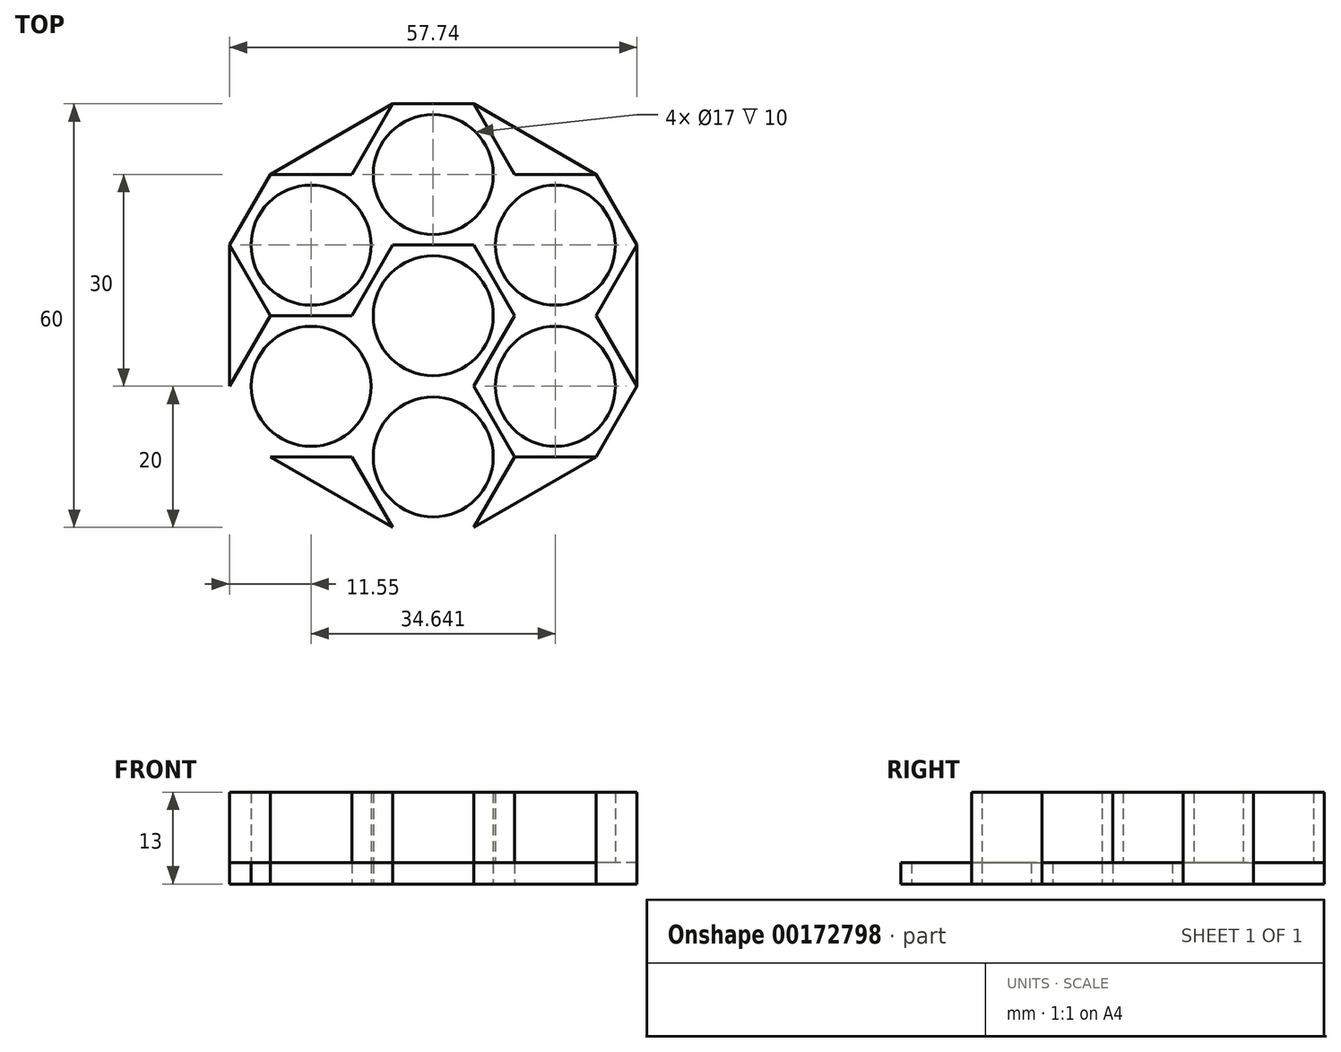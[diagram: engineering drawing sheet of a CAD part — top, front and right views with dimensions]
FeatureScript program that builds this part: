
annotation { "Feature Type Name" : "Feature", "Feature Type Description" : "" }
export const myFeature = defineFeature(function(context is Context, id is Id, definition is map)
    precondition{}
    {
        {
            var Q0;
            Q0=qCreatedBy(makeId("Top.planeOp"),FACE);
            var sketch = newSketch(context, id + "F0", { "sketchPlane" : qUnion([Q0])});
            skCircle(sketch, "E0.cCircle", {"center": v(0, 0) * mm, "radius": 10 * mm, "construction": true});
            skLineSegment(sketch, "E0.0", {"start": v(-5.77, 10) * mm, "end": v(5.77, 10) * mm});
            skLineSegment(sketch, "E0.1", {"start": v(5.77, 10) * mm, "end": v(11.55, 0) * mm});
            skLineSegment(sketch, "E0.2", {"start": v(11.55, 0) * mm, "end": v(5.77, -10) * mm});
            skLineSegment(sketch, "E0.3", {"start": v(5.77, -10) * mm, "end": v(-5.77, -10) * mm});
            skLineSegment(sketch, "E0.4", {"start": v(-5.77, -10) * mm, "end": v(-11.55, 0) * mm});
            skLineSegment(sketch, "E0.5", {"start": v(-11.55, 0) * mm, "end": v(-5.77, 10) * mm});
            skPoint(sketch, "E0.0.midPoint", {"position": v(0, 10) * mm});
            skCircle(sketch, "E1.cCircle", {"center": v(17.32, -10) * mm, "radius": 10 * mm, "construction": true});
            skLineSegment(sketch, "E1.0", {"start": v(11.55, 0) * mm, "end": v(23.1, 0) * mm});
            skLineSegment(sketch, "E1.1", {"start": v(23.1, 0) * mm, "end": v(28.87, -10) * mm});
            skLineSegment(sketch, "E1.2", {"start": v(28.87, -10) * mm, "end": v(23.1, -20) * mm});
            skLineSegment(sketch, "E1.3", {"start": v(23.1, -20) * mm, "end": v(11.55, -20) * mm});
            skLineSegment(sketch, "E1.4", {"start": v(11.55, -20) * mm, "end": v(5.77, -10) * mm});
            skLineSegment(sketch, "E1.5", {"start": v(5.77, -10) * mm, "end": v(11.55, 0) * mm});
            skPoint(sketch, "E1.0.midPoint", {"position": v(17.32, 0) * mm});
            skCircle(sketch, "E2.cCircle", {"center": v(17.32, 10) * mm, "radius": 10 * mm, "construction": true});
            skLineSegment(sketch, "E2.0", {"start": v(11.55, 20) * mm, "end": v(23.1, 20) * mm});
            skLineSegment(sketch, "E2.1", {"start": v(23.1, 20) * mm, "end": v(28.87, 10) * mm});
            skLineSegment(sketch, "E2.2", {"start": v(28.87, 10) * mm, "end": v(23.1, 0) * mm});
            skLineSegment(sketch, "E2.3", {"start": v(23.1, 0) * mm, "end": v(11.55, 0) * mm});
            skLineSegment(sketch, "E2.4", {"start": v(11.55, 0) * mm, "end": v(5.77, 10) * mm});
            skLineSegment(sketch, "E2.5", {"start": v(5.77, 10) * mm, "end": v(11.55, 20) * mm});
            skPoint(sketch, "E2.0.midPoint", {"position": v(17.32, 20) * mm});
            skCircle(sketch, "E3.cCircle", {"center": v(0, 20) * mm, "radius": 10 * mm, "construction": true});
            skLineSegment(sketch, "E3.0", {"start": v(-5.77, 30) * mm, "end": v(5.77, 30) * mm});
            skLineSegment(sketch, "E3.1", {"start": v(5.77, 30) * mm, "end": v(11.55, 20) * mm});
            skLineSegment(sketch, "E3.2", {"start": v(11.55, 20) * mm, "end": v(5.77, 10) * mm});
            skLineSegment(sketch, "E3.3", {"start": v(5.77, 10) * mm, "end": v(-5.77, 10) * mm});
            skLineSegment(sketch, "E3.4", {"start": v(-5.77, 10) * mm, "end": v(-11.55, 20) * mm});
            skLineSegment(sketch, "E3.5", {"start": v(-11.55, 20) * mm, "end": v(-5.77, 30) * mm});
            skPoint(sketch, "E3.0.midPoint", {"position": v(0, 30) * mm});
            skCircle(sketch, "E4.cCircle", {"center": v(-17.32, 10) * mm, "radius": 10 * mm, "construction": true});
            skLineSegment(sketch, "E4.0", {"start": v(-23.1, 20) * mm, "end": v(-11.55, 20) * mm});
            skLineSegment(sketch, "E4.1", {"start": v(-11.55, 20) * mm, "end": v(-5.77, 10) * mm});
            skLineSegment(sketch, "E4.2", {"start": v(-5.77, 10) * mm, "end": v(-11.55, 0) * mm});
            skLineSegment(sketch, "E4.3", {"start": v(-11.55, 0) * mm, "end": v(-23.1, 0) * mm});
            skLineSegment(sketch, "E4.4", {"start": v(-23.1, 0) * mm, "end": v(-28.87, 10) * mm});
            skLineSegment(sketch, "E4.5", {"start": v(-28.87, 10) * mm, "end": v(-23.1, 20) * mm});
            skPoint(sketch, "E4.0.midPoint", {"position": v(-17.32, 20) * mm});
            skCircle(sketch, "E5.cCircle", {"center": v(-17.32, -10) * mm, "radius": 10 * mm, "construction": true});
            skLineSegment(sketch, "E5.0", {"start": v(-23.1, 0) * mm, "end": v(-11.55, 0) * mm});
            skLineSegment(sketch, "E5.1", {"start": v(-11.55, 0) * mm, "end": v(-5.77, -10) * mm});
            skLineSegment(sketch, "E5.2", {"start": v(-5.77, -10) * mm, "end": v(-11.55, -20) * mm});
            skLineSegment(sketch, "E5.3", {"start": v(-11.55, -20) * mm, "end": v(-23.1, -20) * mm});
            skLineSegment(sketch, "E5.4", {"start": v(-23.1, -20) * mm, "end": v(-28.87, -10) * mm});
            skLineSegment(sketch, "E5.5", {"start": v(-28.87, -10) * mm, "end": v(-23.1, 0) * mm});
            skPoint(sketch, "E5.0.midPoint", {"position": v(-17.32, 0) * mm});
            skCircle(sketch, "E6.cCircle", {"center": v(0, -20) * mm, "radius": 10 * mm, "construction": true});
            skLineSegment(sketch, "E6.0", {"start": v(-5.77, -10) * mm, "end": v(5.77, -10) * mm});
            skLineSegment(sketch, "E6.1", {"start": v(5.77, -10) * mm, "end": v(11.55, -20) * mm});
            skLineSegment(sketch, "E6.2", {"start": v(11.55, -20) * mm, "end": v(5.77, -30) * mm});
            skLineSegment(sketch, "E6.3", {"start": v(5.77, -30) * mm, "end": v(-5.77, -30) * mm});
            skLineSegment(sketch, "E6.4", {"start": v(-5.77, -30) * mm, "end": v(-11.55, -20) * mm});
            skLineSegment(sketch, "E6.5", {"start": v(-11.55, -20) * mm, "end": v(-5.77, -10) * mm});
            skPoint(sketch, "E6.0.midPoint", {"position": v(0, -10) * mm});
            skLineSegment(sketch, "E7", {"start": v(-28.87, 10) * mm, "end": v(-28.87, -10) * mm});
            skLineSegment(sketch, "E8", {"start": v(-23.1, -20) * mm, "end": v(-5.77, -30) * mm});
            skLineSegment(sketch, "E9", {"start": v(5.77, -30) * mm, "end": v(23.1, -20) * mm});
            skLineSegment(sketch, "E10", {"start": v(28.87, -10) * mm, "end": v(28.87, 10) * mm});
            skLineSegment(sketch, "E11", {"start": v(23.1, 20) * mm, "end": v(5.77, 30) * mm});
            skLineSegment(sketch, "E12", {"start": v(-5.77, 30) * mm, "end": v(-23.1, 20) * mm});
            skCircle(sketch, "E13.0", {"center": v(-17.32, 10) * mm, "radius": 8.5 * mm});
            skCircle(sketch, "E14.0", {"center": v(0, 20) * mm, "radius": 8.5 * mm});
            skCircle(sketch, "E15.0", {"center": v(17.32, 10) * mm, "radius": 8.5 * mm});
            skCircle(sketch, "E16.0", {"center": v(17.32, -10) * mm, "radius": 8.5 * mm});
            skCircle(sketch, "E17.0", {"center": v(0, -20) * mm, "radius": 8.5 * mm});
            skCircle(sketch, "E18.0", {"center": v(-17.32, -10) * mm, "radius": 8.5 * mm});
            skCircle(sketch, "E19.0", {"center": v(0, 0) * mm, "radius": 8.5 * mm});
            skSolve(sketch);
        }
        {
            var Q0;
            Q0=makeQuery(id+"F0.imprint","IMPRINT",FACE,{"disambiguationData":[TD([[makeQuery(id+"F0.imprint","IMPRINT",EDGE,{"derivedFrom":sQuery(id+"F0.wireOp",EDGE,"E3.5")}),1.0]])]});
            var Q1;
            Q1=makeQuery(id+"F0.imprint","IMPRINT",FACE,{"disambiguationData":[TD([[makeQuery(id+"F0.imprint","IMPRINT",EDGE,{"derivedFrom":sQuery(id+"F0.wireOp",EDGE,"E2.0")}),1.0]])]});
            var Q2;
            Q2=makeQuery(id+"F0.imprint","IMPRINT",FACE,{"disambiguationData":[TD([[makeQuery(id+"F0.imprint","IMPRINT",EDGE,{"derivedFrom":sQuery(id+"F0.wireOp",EDGE,"E2.0")}),-1.0]])]});
            var Q3;
            Q3=makeQuery(id+"F0.imprint","IMPRINT",FACE,{"disambiguationData":[TD([[makeQuery(id+"F0.imprint","IMPRINT",EDGE,{"derivedFrom":sQuery(id+"F0.wireOp",EDGE,"E5.3")}),1.0]])]});
            var Q4;
            Q4=makeQuery(id+"F0.imprint","IMPRINT",FACE,{"disambiguationData":[TD([[makeQuery(id+"F0.imprint","IMPRINT",EDGE,{"derivedFrom":sQuery(id+"F0.wireOp",EDGE,"E1.1")}),-1.0]])]});
            var Q5;
            Q5=makeQuery(id+"F0.imprint","IMPRINT",FACE,{"disambiguationData":[TD([[makeQuery(id+"F0.imprint","IMPRINT",EDGE,{"derivedFrom":sQuery(id+"F0.wireOp",EDGE,"E1.1")}),1.0]])]});
            var Q6;
            Q6=makeQuery(id+"F0.imprint","IMPRINT",FACE,{"disambiguationData":[TD([[makeQuery(id+"F0.imprint","IMPRINT",EDGE,{"derivedFrom":sQuery(id+"F0.wireOp",EDGE,"E4.4")}),1.0]])]});
            var Q7;
            Q7=makeQuery(id+"F0.imprint","IMPRINT",FACE,{"disambiguationData":[TD([[makeQuery(id+"F0.imprint","IMPRINT",EDGE,{"derivedFrom":sQuery(id+"F0.wireOp",EDGE,"E3.0")}),-1.0]])]});
            var Q8;
            Q8=makeQuery(id+"F0.imprint","IMPRINT",FACE,{"disambiguationData":[TD([[makeQuery(id+"F0.imprint","IMPRINT",EDGE,{"derivedFrom":sQuery(id+"F0.wireOp",EDGE,"E1.5")}),1.0]])]});
            var Q9;
            Q9=makeQuery(id+"F0.imprint","IMPRINT",FACE,{"disambiguationData":[TD([[makeQuery(id+"F0.imprint","IMPRINT",EDGE,{"derivedFrom":sQuery(id+"F0.wireOp",EDGE,"E6.0")}),-1.0]])]});
            var Q10;
            Q10=makeQuery(id+"F0.imprint","IMPRINT",FACE,{"disambiguationData":[TD([[makeQuery(id+"F0.imprint","IMPRINT",EDGE,{"derivedFrom":sQuery(id+"F0.wireOp",EDGE,"E1.3")}),1.0]])]});
            var Q11;
            Q11=makeQuery(id+"F0.imprint","IMPRINT",FACE,{"disambiguationData":[TD([[makeQuery(id+"F0.imprint","IMPRINT",EDGE,{"derivedFrom":sQuery(id+"F0.wireOp",EDGE,"E5.0")}),-1.0]])]});
            var Q12;
            Q12=makeQuery(id+"F0.imprint","IMPRINT",FACE,{"disambiguationData":[TD([[makeQuery(id+"F0.imprint","IMPRINT",EDGE,{"derivedFrom":sQuery(id+"F0.wireOp",EDGE,"E4.0")}),-1.0]])]});
            var Q13;
            Q13=makeQuery(id+"F0.imprint","IMPRINT",FACE,{"disambiguationData":[TD([[makeQuery(id+"F0.imprint","IMPRINT",EDGE,{"derivedFrom":sQuery(id+"F0.wireOp",EDGE,"E14.0")}),1.0]])]});
            var Q14;
            Q14=makeQuery(id+"F0.imprint","IMPRINT",FACE,{"disambiguationData":[TD([[makeQuery(id+"F0.imprint","IMPRINT",EDGE,{"derivedFrom":sQuery(id+"F0.wireOp",EDGE,"E15.0")}),1.0]])]});
            var Q15;
            Q15=makeQuery(id+"F0.imprint","IMPRINT",FACE,{"disambiguationData":[TD([[makeQuery(id+"F0.imprint","IMPRINT",EDGE,{"derivedFrom":sQuery(id+"F0.wireOp",EDGE,"E19.0")}),1.0]])]});
            var Q16;
            Q16=makeQuery(id+"F0.imprint","IMPRINT",FACE,{"disambiguationData":[TD([[makeQuery(id+"F0.imprint","IMPRINT",EDGE,{"derivedFrom":sQuery(id+"F0.wireOp",EDGE,"E16.0")}),1.0]])]});
            var Q17;
            Q17=makeQuery(id+"F0.imprint","IMPRINT",FACE,{"disambiguationData":[TD([[makeQuery(id+"F0.imprint","IMPRINT",EDGE,{"derivedFrom":sQuery(id+"F0.wireOp",EDGE,"E17.0")}),1.0]])]});
            var Q18;
            Q18=makeQuery(id+"F0.imprint","IMPRINT",FACE,{"disambiguationData":[TD([[makeQuery(id+"F0.imprint","IMPRINT",EDGE,{"derivedFrom":sQuery(id+"F0.wireOp",EDGE,"E18.0")}),1.0]])]});
            var Q19;
            Q19=makeQuery(id+"F0.imprint","IMPRINT",FACE,{"disambiguationData":[TD([[makeQuery(id+"F0.imprint","IMPRINT",EDGE,{"derivedFrom":sQuery(id+"F0.wireOp",EDGE,"E13.0")}),1.0]])]});
            extrude(context, id + "F1", {"entities" : qUnion([Q0, Q1, Q2, Q3, Q4, Q5, Q6, Q7, Q8, Q9, Q10, Q11, Q12, Q13, Q14, Q15, Q16, Q17, Q18, Q19]), "depth" : 3 * mm});
        }
        {
            var Q0;
            Q0=makeQuery(id+"F0.imprint","IMPRINT",FACE,{"disambiguationData":[TD([[makeQuery(id+"F0.imprint","IMPRINT",EDGE,{"derivedFrom":sQuery(id+"F0.wireOp",EDGE,"E1.5")}),1.0]])]});
            var Q1;
            Q1=makeQuery(id+"F0.imprint","IMPRINT",FACE,{"disambiguationData":[TD([[makeQuery(id+"F0.imprint","IMPRINT",EDGE,{"derivedFrom":sQuery(id+"F0.wireOp",EDGE,"E5.0")}),-1.0]])]});
            var Q2;
            Q2=makeQuery(id+"F0.imprint","IMPRINT",FACE,{"disambiguationData":[TD([[makeQuery(id+"F0.imprint","IMPRINT",EDGE,{"derivedFrom":sQuery(id+"F0.wireOp",EDGE,"E3.0")}),-1.0]])]});
            var Q3;
            Q3=makeQuery(id+"F0.imprint","IMPRINT",FACE,{"disambiguationData":[TD([[makeQuery(id+"F0.imprint","IMPRINT",EDGE,{"derivedFrom":sQuery(id+"F0.wireOp",EDGE,"E6.0")}),-1.0]])]});
            var Q4;
            Q4=makeQuery(id+"F0.imprint","IMPRINT",FACE,{"disambiguationData":[TD([[makeQuery(id+"F0.imprint","IMPRINT",EDGE,{"derivedFrom":sQuery(id+"F0.wireOp",EDGE,"E1.1")}),-1.0]])]});
            var Q5;
            Q5=makeQuery(id+"F0.imprint","IMPRINT",FACE,{"disambiguationData":[TD([[makeQuery(id+"F0.imprint","IMPRINT",EDGE,{"derivedFrom":sQuery(id+"F0.wireOp",EDGE,"E2.0")}),-1.0]])]});
            var Q6;
            Q6=makeQuery(id+"F0.imprint","IMPRINT",FACE,{"disambiguationData":[TD([[makeQuery(id+"F0.imprint","IMPRINT",EDGE,{"derivedFrom":sQuery(id+"F0.wireOp",EDGE,"E4.0")}),-1.0]])]});
            extrude(context, id + "F2", {"entities" : qUnion([Q0, Q1, Q2, Q3, Q4, Q5, Q6]), "operationType" : NewBodyOperationType.ADD, "depth" : 13 * mm});
        }
    });
